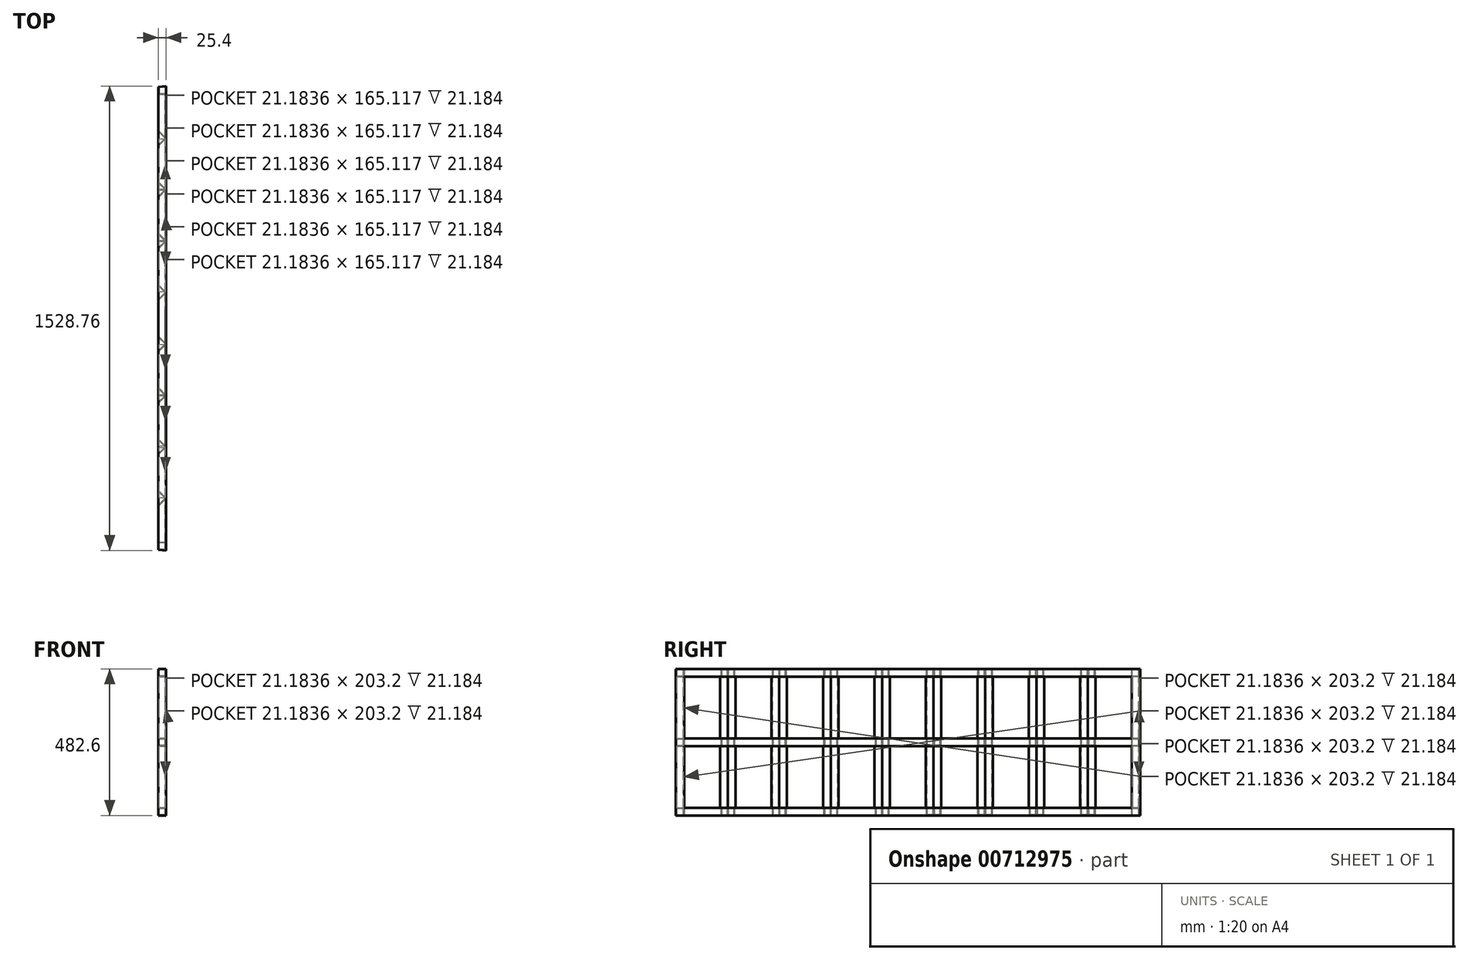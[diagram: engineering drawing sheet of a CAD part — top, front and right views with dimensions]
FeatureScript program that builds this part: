
annotation { "Feature Type Name" : "Feature", "Feature Type Description" : "" }
export const myFeature = defineFeature(function(context is Context, id is Id, definition is map)
    precondition{}
    {
        {
            var Q0;
            Q0=qCreatedBy(makeId("Front.planeOp"),FACE);
            var sketch = newSketch(context, id + "F0", { "sketchPlane" : qUnion([Q0])});
            skLineSegment(sketch, "E0.bottom", {"start": v(-12.7, -211.82) * mm, "end": v(12.7, -211.82) * mm});
            skLineSegment(sketch, "E0.top", {"start": v(-12.7, -237.22) * mm, "end": v(12.7, -237.22) * mm});
            skLineSegment(sketch, "E0.left", {"start": v(-12.7, -211.82) * mm, "end": v(-12.7, -237.22) * mm});
            skLineSegment(sketch, "E0.right", {"start": v(12.7, -211.82) * mm, "end": v(12.7, -237.22) * mm});
            skPoint(sketch, "E0.middle", {"position": v(0, -224.52) * mm});
            skLineSegment(sketch, "E1.0", {"start": v(-10.6, -213.93) * mm, "end": v(10.6, -213.93) * mm});
            skLineSegment(sketch, "E1.1", {"start": v(-10.6, -213.93) * mm, "end": v(-10.6, -235.1) * mm});
            skLineSegment(sketch, "E1.2", {"start": v(-10.6, -235.1) * mm, "end": v(10.6, -235.1) * mm});
            skLineSegment(sketch, "E1.3", {"start": v(10.6, -213.93) * mm, "end": v(10.6, -235.1) * mm});
            skLineSegment(sketch, "E2.1.0.0", {"start": v(12.7, 16.78) * mm, "end": v(12.7, -8.62) * mm});
            skLineSegment(sketch, "E2.1.0.1", {"start": v(-12.7, 16.78) * mm, "end": v(-12.7, -8.62) * mm});
            skLineSegment(sketch, "E2.1.0.2", {"start": v(-12.7, -8.62) * mm, "end": v(12.7, -8.62) * mm});
            skLineSegment(sketch, "E2.1.0.3", {"start": v(-12.7, 16.78) * mm, "end": v(12.7, 16.78) * mm});
            skLineSegment(sketch, "E2.1.0.4", {"start": v(-10.6, -6.5) * mm, "end": v(10.6, -6.5) * mm});
            skPoint(sketch, "E2.1.0.5", {"position": v(0, 4.08) * mm});
            skLineSegment(sketch, "E2.1.0.6", {"start": v(10.6, 14.67) * mm, "end": v(10.6, -6.5) * mm});
            skLineSegment(sketch, "E2.1.0.7", {"start": v(-10.6, 14.67) * mm, "end": v(10.6, 14.67) * mm});
            skLineSegment(sketch, "E2.1.0.8", {"start": v(-10.6, 14.67) * mm, "end": v(-10.6, -6.5) * mm});
            skLineSegment(sketch, "E2.2.0.0", {"start": v(12.7, 245.38) * mm, "end": v(12.7, 219.98) * mm});
            skLineSegment(sketch, "E2.2.0.1", {"start": v(-12.7, 245.38) * mm, "end": v(-12.7, 219.98) * mm});
            skLineSegment(sketch, "E2.2.0.2", {"start": v(-12.7, 219.98) * mm, "end": v(12.7, 219.98) * mm});
            skLineSegment(sketch, "E2.2.0.3", {"start": v(-12.7, 245.38) * mm, "end": v(12.7, 245.38) * mm});
            skLineSegment(sketch, "E2.2.0.4", {"start": v(-10.6, 222.1) * mm, "end": v(10.6, 222.1) * mm});
            skPoint(sketch, "E2.2.0.5", {"position": v(0, 232.68) * mm});
            skLineSegment(sketch, "E2.2.0.6", {"start": v(10.6, 243.27) * mm, "end": v(10.6, 222.1) * mm});
            skLineSegment(sketch, "E2.2.0.7", {"start": v(-10.6, 243.27) * mm, "end": v(10.6, 243.27) * mm});
            skLineSegment(sketch, "E2.2.0.8", {"start": v(-10.6, 243.27) * mm, "end": v(-10.6, 222.1) * mm});
            skLineSegment(sketch, "E2.direction1", {"start": v(0, -224.52) * mm, "end": v(0, 4.08) * mm, "construction": true});
            skSolve(sketch);
        }
        {
            var Q0;
            Q0=makeQuery(id+"F0.imprint","IMPRINT",FACE,{"disambiguationData":[TD([[makeQuery(id+"F0.imprint","IMPRINT",EDGE,{"derivedFrom":sQuery(id+"F0.wireOp",EDGE,"E2.2.0.0")}),-1.0]])]});
            var Q1;
            Q1=makeQuery(id+"F0.imprint","IMPRINT",FACE,{"disambiguationData":[TD([[makeQuery(id+"F0.imprint","IMPRINT",EDGE,{"derivedFrom":sQuery(id+"F0.wireOp",EDGE,"E2.1.0.0")}),-1.0]])]});
            var Q2;
            Q2=makeQuery(id+"F0.imprint","IMPRINT",FACE,{"disambiguationData":[TD([[makeQuery(id+"F0.imprint","IMPRINT",EDGE,{"derivedFrom":sQuery(id+"F0.wireOp",EDGE,"E0.bottom")}),-1.0]])]});
            extrude(context, id + "F1", {"entities" : qUnion([Q0, Q1, Q2]), "endBound" : BoundingType.SYMMETRIC, "depth" : 1524 * mm, "offsetDistance" : 25.4 * mm});
        }
        {
            var Q0;
            Q0=makeQuery(id+"F1.opExtrude","SWEPT_FACE",FACE,{"disambiguationData":[OSD([sQuery(id+"F0.wireOp",EDGE,"E2.2.0.3")])]});
            var sketch = newSketch(context, id + "F2", { "sketchPlane" : qUnion([Q0])});
            skLineSegment(sketch, "E3.bottom", {"start": v(12.7, 762) * mm, "end": v(-12.7, 762) * mm});
            skLineSegment(sketch, "E3.top", {"start": v(12.7, 736.6) * mm, "end": v(-12.7, 736.6) * mm});
            skLineSegment(sketch, "E3.left", {"start": v(12.7, 762) * mm, "end": v(12.7, 736.6) * mm});
            skLineSegment(sketch, "E3.right", {"start": v(-12.7, 762) * mm, "end": v(-12.7, 736.6) * mm});
            skLineSegment(sketch, "E4.bottom", {"start": v(-12.7, -762) * mm, "end": v(12.7, -762) * mm});
            skLineSegment(sketch, "E4.top", {"start": v(-12.7, -736.6) * mm, "end": v(12.7, -736.6) * mm});
            skLineSegment(sketch, "E4.left", {"start": v(-12.7, -762) * mm, "end": v(-12.7, -736.6) * mm});
            skLineSegment(sketch, "E4.right", {"start": v(12.7, -762) * mm, "end": v(12.7, -736.6) * mm});
            skLineSegment(sketch, "E5.0", {"start": v(10.6, 759.9) * mm, "end": v(-10.6, 759.9) * mm});
            skLineSegment(sketch, "E5.1", {"start": v(10.6, 759.9) * mm, "end": v(10.6, 738.7) * mm});
            skLineSegment(sketch, "E5.2", {"start": v(10.6, 738.7) * mm, "end": v(-10.6, 738.7) * mm});
            skLineSegment(sketch, "E5.3", {"start": v(-10.6, 759.9) * mm, "end": v(-10.6, 738.7) * mm});
            skLineSegment(sketch, "E6.0", {"start": v(-10.6, -738.7) * mm, "end": v(10.6, -738.7) * mm});
            skLineSegment(sketch, "E6.1", {"start": v(-10.6, -759.9) * mm, "end": v(-10.6, -738.7) * mm});
            skLineSegment(sketch, "E6.2", {"start": v(-10.6, -759.9) * mm, "end": v(10.6, -759.9) * mm});
            skLineSegment(sketch, "E6.3", {"start": v(10.6, -759.9) * mm, "end": v(10.6, -738.7) * mm});
            skSolve(sketch);
        }
        {
            var Q0;
            Q0 = qSketchRegion(id + "F2", true);
            extrude(context, id + "F3", {"entities" : qUnion([Q0]), "operationType" : NewBodyOperationType.ADD, "oppositeDirection" : true, "depth" : 482.6 * mm, "offsetDistance" : 25.4 * mm});
        }
        {
            var Q0;
            Q0=makeQuery(id+"F1.opExtrude","SWEPT_FACE",FACE,{"disambiguationData":[OSD([sQuery(id+"F0.wireOp",EDGE,"E2.2.0.3")])]});
            var sketch = newSketch(context, id + "F4", { "sketchPlane" : qUnion([Q0])});
            skLineSegment(sketch, "E7", {"start": v(-12.7, 762) * mm, "end": v(12.7, 764.38) * mm});
            skLineSegment(sketch, "E8", {"start": v(12.7, 764.38) * mm, "end": v(12.7, 762) * mm});
            skLineSegment(sketch, "E9", {"start": v(12.7, 762) * mm, "end": v(-12.7, 762) * mm});
            skLineSegment(sketch, "E10", {"start": v(-12.7, 618.07) * mm, "end": v(12.7, 592.67) * mm});
            skLineSegment(sketch, "E11", {"start": v(12.7, 592.67) * mm, "end": v(-12.7, 567.27) * mm});
            skLineSegment(sketch, "E12.0", {"start": v(9.72, 592.67) * mm, "end": v(-12.7, 570.25) * mm});
            skLineSegment(sketch, "E12.1", {"start": v(-12.7, 615.09) * mm, "end": v(9.72, 592.67) * mm});
            skLineSegment(sketch, "E13", {"start": v(-12.7, 618.07) * mm, "end": v(-12.7, 615.09) * mm});
            skLineSegment(sketch, "E14", {"start": v(-12.7, 567.27) * mm, "end": v(-12.7, 570.25) * mm});
            skLineSegment(sketch, "E15.1.0.0", {"start": v(-12.7, 448.73) * mm, "end": v(12.7, 423.33) * mm});
            skLineSegment(sketch, "E15.1.0.1", {"start": v(12.7, 423.33) * mm, "end": v(-12.7, 397.93) * mm});
            skLineSegment(sketch, "E15.1.0.2", {"start": v(9.72, 423.33) * mm, "end": v(-12.7, 400.91) * mm});
            skLineSegment(sketch, "E15.1.0.3", {"start": v(-12.7, 445.75) * mm, "end": v(9.72, 423.33) * mm});
            skLineSegment(sketch, "E15.1.0.4", {"start": v(-12.7, 448.73) * mm, "end": v(-12.7, 445.75) * mm});
            skLineSegment(sketch, "E15.1.0.5", {"start": v(-12.7, 397.93) * mm, "end": v(-12.7, 400.91) * mm});
            skLineSegment(sketch, "E15.2.0.0", {"start": v(-12.7, 279.4) * mm, "end": v(12.7, 254) * mm});
            skLineSegment(sketch, "E15.2.0.1", {"start": v(12.7, 254) * mm, "end": v(-12.7, 228.6) * mm});
            skLineSegment(sketch, "E15.2.0.2", {"start": v(9.72, 254) * mm, "end": v(-12.7, 231.58) * mm});
            skLineSegment(sketch, "E15.2.0.3", {"start": v(-12.7, 276.42) * mm, "end": v(9.72, 254) * mm});
            skLineSegment(sketch, "E15.2.0.4", {"start": v(-12.7, 279.4) * mm, "end": v(-12.7, 276.42) * mm});
            skLineSegment(sketch, "E15.2.0.5", {"start": v(-12.7, 228.6) * mm, "end": v(-12.7, 231.58) * mm});
            skLineSegment(sketch, "E15.3.0.0", {"start": v(-12.7, 110.07) * mm, "end": v(12.7, 84.67) * mm});
            skLineSegment(sketch, "E15.3.0.1", {"start": v(12.7, 84.67) * mm, "end": v(-12.7, 59.27) * mm});
            skLineSegment(sketch, "E15.3.0.2", {"start": v(9.72, 84.67) * mm, "end": v(-12.7, 62.25) * mm});
            skLineSegment(sketch, "E15.3.0.3", {"start": v(-12.7, 107.09) * mm, "end": v(9.72, 84.67) * mm});
            skLineSegment(sketch, "E15.3.0.4", {"start": v(-12.7, 110.07) * mm, "end": v(-12.7, 107.09) * mm});
            skLineSegment(sketch, "E15.3.0.5", {"start": v(-12.7, 59.27) * mm, "end": v(-12.7, 62.25) * mm});
            skLineSegment(sketch, "E15.direction1", {"start": v(-12.7, 567.27) * mm, "end": v(-12.7, 397.93) * mm, "construction": true});
            skLineSegment(sketch, "E16.MirrorCS", {"start": v(-12.7, -618.07) * mm, "end": v(-12.7, -615.09) * mm});
            skLineSegment(sketch, "E17.MirrorCS", {"start": v(-12.7, -228.6) * mm, "end": v(-12.7, -231.58) * mm});
            skLineSegment(sketch, "E18.MirrorCS", {"start": v(-12.7, -567.27) * mm, "end": v(-12.7, -570.25) * mm});
            skLineSegment(sketch, "E19.MirrorCS", {"start": v(-12.7, -618.07) * mm, "end": v(12.7, -592.67) * mm});
            skLineSegment(sketch, "E20.MirrorCS", {"start": v(12.7, -764.38) * mm, "end": v(12.7, -762) * mm});
            skLineSegment(sketch, "E21.MirrorCS", {"start": v(-12.7, -762) * mm, "end": v(12.7, -764.38) * mm});
            skLineSegment(sketch, "E22.MirrorCS", {"start": v(-12.7, -397.93) * mm, "end": v(-12.7, -400.91) * mm});
            skLineSegment(sketch, "E23.MirrorCS", {"start": v(12.7, -254) * mm, "end": v(-12.7, -228.6) * mm});
            skLineSegment(sketch, "E24.MirrorCS", {"start": v(-12.7, -448.73) * mm, "end": v(-12.7, -445.75) * mm});
            skLineSegment(sketch, "E25.MirrorCS", {"start": v(9.72, -254) * mm, "end": v(-12.7, -231.58) * mm});
            skLineSegment(sketch, "E26.MirrorCS", {"start": v(-12.7, -107.09) * mm, "end": v(9.72, -84.67) * mm});
            skLineSegment(sketch, "E27.MirrorCS", {"start": v(-12.7, -445.75) * mm, "end": v(9.72, -423.33) * mm});
            skLineSegment(sketch, "E28.MirrorCS", {"start": v(9.72, -423.33) * mm, "end": v(-12.7, -400.91) * mm});
            skLineSegment(sketch, "E29.MirrorCS", {"start": v(-12.7, -448.73) * mm, "end": v(12.7, -423.33) * mm});
            skLineSegment(sketch, "E30.MirrorCS", {"start": v(-12.7, -615.09) * mm, "end": v(9.72, -592.67) * mm});
            skLineSegment(sketch, "E31.MirrorCS", {"start": v(9.72, -592.67) * mm, "end": v(-12.7, -570.25) * mm});
            skLineSegment(sketch, "E32.MirrorCS", {"start": v(12.7, -762) * mm, "end": v(-12.7, -762) * mm});
            skLineSegment(sketch, "E33.MirrorCS", {"start": v(9.72, -84.67) * mm, "end": v(-12.7, -62.25) * mm});
            skLineSegment(sketch, "E34.MirrorCS", {"start": v(-12.7, -276.42) * mm, "end": v(9.72, -254) * mm});
            skLineSegment(sketch, "E35.MirrorCS", {"start": v(-12.7, -59.27) * mm, "end": v(-12.7, -62.25) * mm});
            skLineSegment(sketch, "E36.MirrorCS", {"start": v(-12.7, -279.4) * mm, "end": v(-12.7, -276.42) * mm});
            skLineSegment(sketch, "E37.MirrorCS", {"start": v(-12.7, -110.07) * mm, "end": v(-12.7, -107.09) * mm});
            skLineSegment(sketch, "E38.MirrorCS", {"start": v(12.7, -592.67) * mm, "end": v(-12.7, -567.27) * mm});
            skLineSegment(sketch, "E39.MirrorCS", {"start": v(-12.7, -110.07) * mm, "end": v(12.7, -84.67) * mm});
            skLineSegment(sketch, "E40.MirrorCS", {"start": v(12.7, -423.33) * mm, "end": v(-12.7, -397.93) * mm});
            skLineSegment(sketch, "E41.MirrorCS", {"start": v(-12.7, -279.4) * mm, "end": v(12.7, -254) * mm});
            skLineSegment(sketch, "E42.MirrorCS", {"start": v(-12.7, -567.27) * mm, "end": v(-12.7, -397.93) * mm, "construction": true});
            skLineSegment(sketch, "E43.MirrorCS", {"start": v(12.7, -84.67) * mm, "end": v(-12.7, -59.27) * mm});
            skSolve(sketch);
        }
        {
            var Q0;
            Q0 = qSketchRegion(id + "F4", true);
            extrude(context, id + "F5", {"entities" : qUnion([Q0]), "operationType" : NewBodyOperationType.ADD, "oppositeDirection" : true, "depth" : 482.6 * mm, "offsetDistance" : 25.4 * mm});
        }
    });
